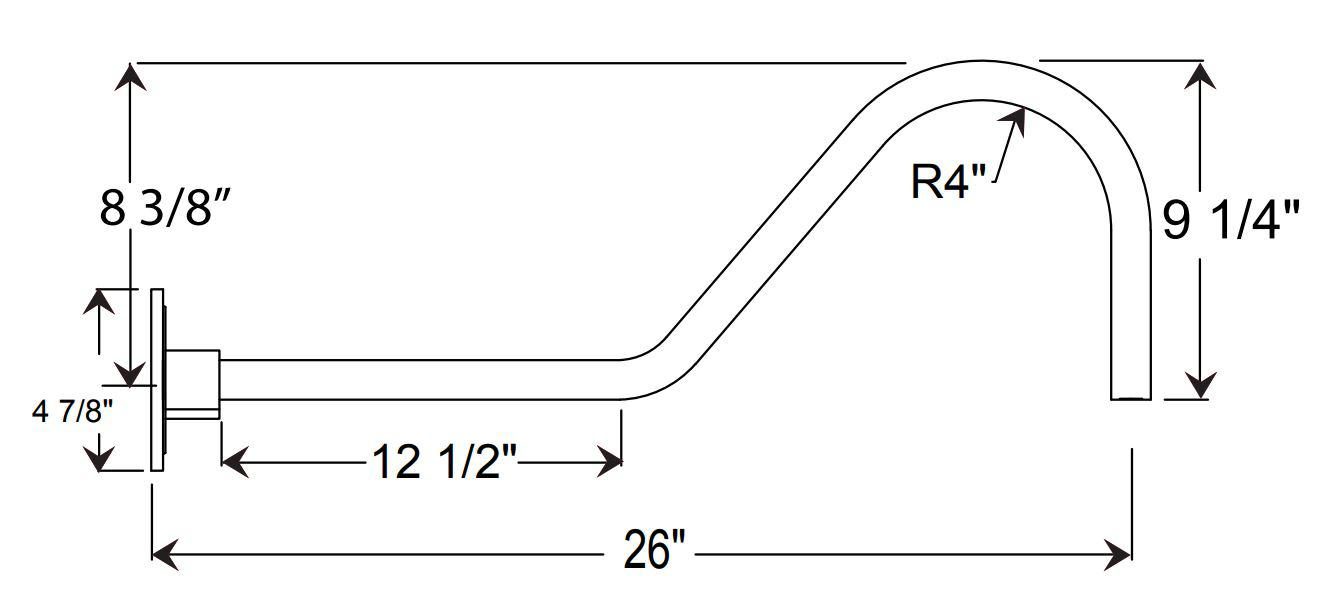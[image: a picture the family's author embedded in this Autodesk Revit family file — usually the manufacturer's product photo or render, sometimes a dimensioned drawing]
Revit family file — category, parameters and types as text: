
# Revit family: OSSD 20,24,36,42 LED
name_source: partatom
category: Lighting Fixtures
units: mm (PartAtom-declared; Revit-internal decimal feet)

## family parameters
Always vertical = Yes
Cut with Voids When Loaded = No
Light Source = Yes
OmniClass Number = 23.80.70.00
OmniClass Title = Lighting
Part Type = Normal
Room Calculation Point = No
Round Connector Dimension = Use Diameter
Shared = No
Work Plane-Based = No

## types (4) — shared parameters
Body Colour = Spun aluminium
Body Material = body
Bulb = BULB
CRI = >90
Canopy Body = body
Color Filter = 16777215
Construction Material = Heavy Duty spun aluminum.
Default Elevation = 0' - 0"
Description = 120-277 Voltage
Dimming = 1%
Dimming Lamp Color Temperature Shift = <None>
Efficiency = 65-125 lumens per watt
INSIDE BODY = Default
Lamp = LED
Life = L70 50,000 hours
Load Classification = Lighting
Manufacturer = ANP Lighting
Power Factor = 1
Tilt Angle = 90.00°
URL = https://www.anplighting.com
Voltage = 277 V
Warranty = 5 year limited warranty
b = 0' - 2"

## per-type parameters (varying)
| type | Apparent Load | Fixture Diameter | Fixture Height | OSSD24 | OSSD30 | OSSD36 | OSSD42 | Photometric Web File | Wattage Comments | Weight | a |
| OSSD24 | 24 VA | 2' - 0" | 1' - 0" | Yes | No | No | No | OSSD30M037LDDW35K.ies | 24W | 18.0 lbs | 0' - 10" |
| OSSD30 | 37 VA | 2' - 0" | 1' - 0" | No | Yes | No | No | OSSD30M037LDDW35K.ies | 37W | 18.0 lbs | 0' - 11" |
| OSSD36 | 37 VA | 3' - 0" | 1' - 6" | No | No | Yes | No | OSSD36M037LDDW35K.ies | 37W | 26.0 lbs | 0' - 10" |
| OSSD42 | 37 VA | 3' - 6" | 1' - 9" | No | No | No | Yes | OSSD42M037LDDW35K.ies | 37W | 32.0 lbs | 0' - 10" |

note: column(s) folded — value = type name in every type: Model

## geometry (parser evidence)
native form markers: Sweep x44
no freeform markers — native parametric forms only
